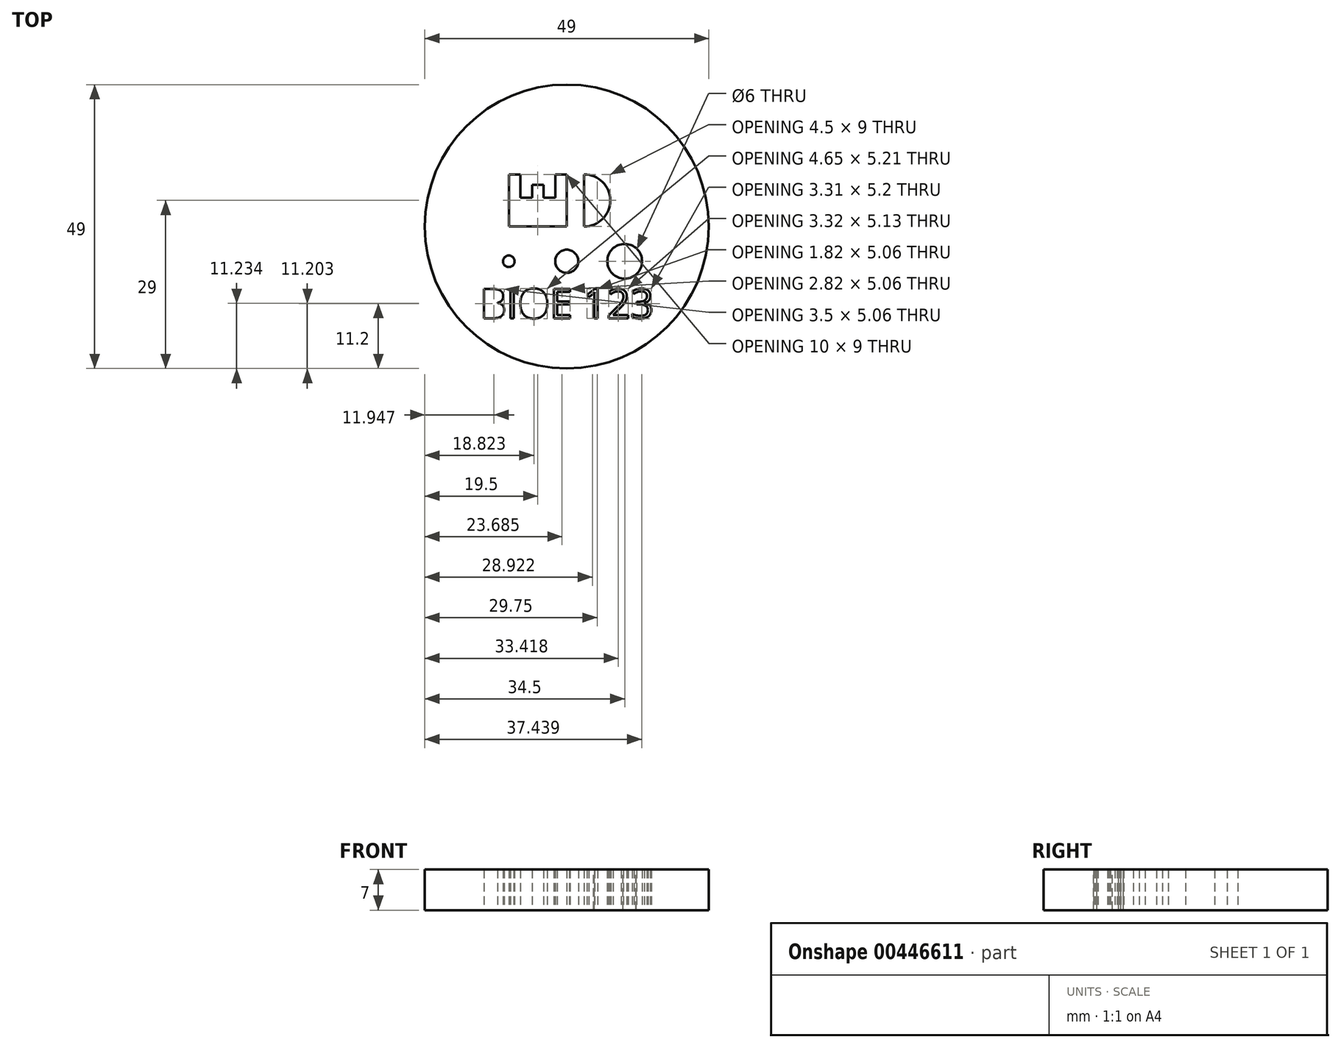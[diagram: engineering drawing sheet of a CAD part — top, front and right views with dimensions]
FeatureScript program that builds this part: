
annotation { "Feature Type Name" : "Feature", "Feature Type Description" : "" }
export const myFeature = defineFeature(function(context is Context, id is Id, definition is map)
    precondition{}
    {
        {
            var Q0;
            Q0=qCreatedBy(makeId("Top.planeOp"),FACE);
            var sketch = newSketch(context, id + "F0", { "sketchPlane" : qUnion([Q0])});
            skCircle(sketch, "E0", {"center": v(0, 0) * mm, "radius": 24.5 * mm});
            skLineSegment(sketch, "E1", {"start": v(0, 0) * mm, "end": v(-10, 0) * mm});
            skLineSegment(sketch, "E2", {"start": v(-10, 0) * mm, "end": v(-10, 9) * mm});
            skLineSegment(sketch, "E3", {"start": v(0, 0) * mm, "end": v(0, 9) * mm});
            skLineSegment(sketch, "E4", {"start": v(0, 0) * mm, "end": v(3, 0) * mm, "construction": true});
            skLineSegment(sketch, "E5", {"start": v(3, 9) * mm, "end": v(3, 0) * mm});
            skArc(sketch, "E6", {"start": v(3, 0) * mm, "mid": v(7.5, 4.5) * mm, "end": v(3, 9) * mm});
            skLineSegment(sketch, "E7", {"start": v(-10, 9) * mm, "end": v(-8, 9) * mm});
            skLineSegment(sketch, "E8", {"start": v(-8, 9) * mm, "end": v(-8, 5) * mm});
            skLineSegment(sketch, "E9", {"start": v(-8, 5) * mm, "end": v(-6, 5) * mm});
            skLineSegment(sketch, "E10", {"start": v(-6, 7.2) * mm, "end": v(-4, 7.2) * mm});
            skLineSegment(sketch, "E11", {"start": v(-4, 7.2) * mm, "end": v(-4, 5) * mm});
            skLineSegment(sketch, "E12", {"start": v(-4, 5) * mm, "end": v(-2, 5) * mm});
            skLineSegment(sketch, "E13", {"start": v(0, 9) * mm, "end": v(-2, 9) * mm});
            skLineSegment(sketch, "E14", {"start": v(-6, 5) * mm, "end": v(-6, 7.2) * mm});
            skLineSegment(sketch, "E15", {"start": v(-2, 5) * mm, "end": v(-2, 9) * mm});
            skCircle(sketch, "E16", {"center": v(0, -6) * mm, "radius": 2 * mm});
            skCircle(sketch, "E17", {"center": v(-10, -6) * mm, "radius": 1 * mm});
            skCircle(sketch, "E18", {"center": v(10, -6) * mm, "radius": 3 * mm});
            skText(sketch, "E19", { "text": "BIOE 123", "fontName": "OpenSans-Regular.ttf"});
            const initialGuessF0  = {"E19": [-0.015, -0.01583, 1, 0, 0.0051]};
            skSetInitialGuess(sketch, initialGuessF0);
            skSolve(sketch);
        }
        {
            var Q0;
            Q0=makeQuery(id+"F0.imprint","IMPRINT",FACE,{"disambiguationData":[TD([[makeQuery(id+"F0.imprint","IMPRINT",EDGE,{"derivedFrom":sQuery(id+"F0.wireOp",EDGE,"E0")}),1.0]])]});
            extrude(context, id + "F1", {"entities" : qUnion([Q0]), "depth" : 7 * mm});
        }
    });
